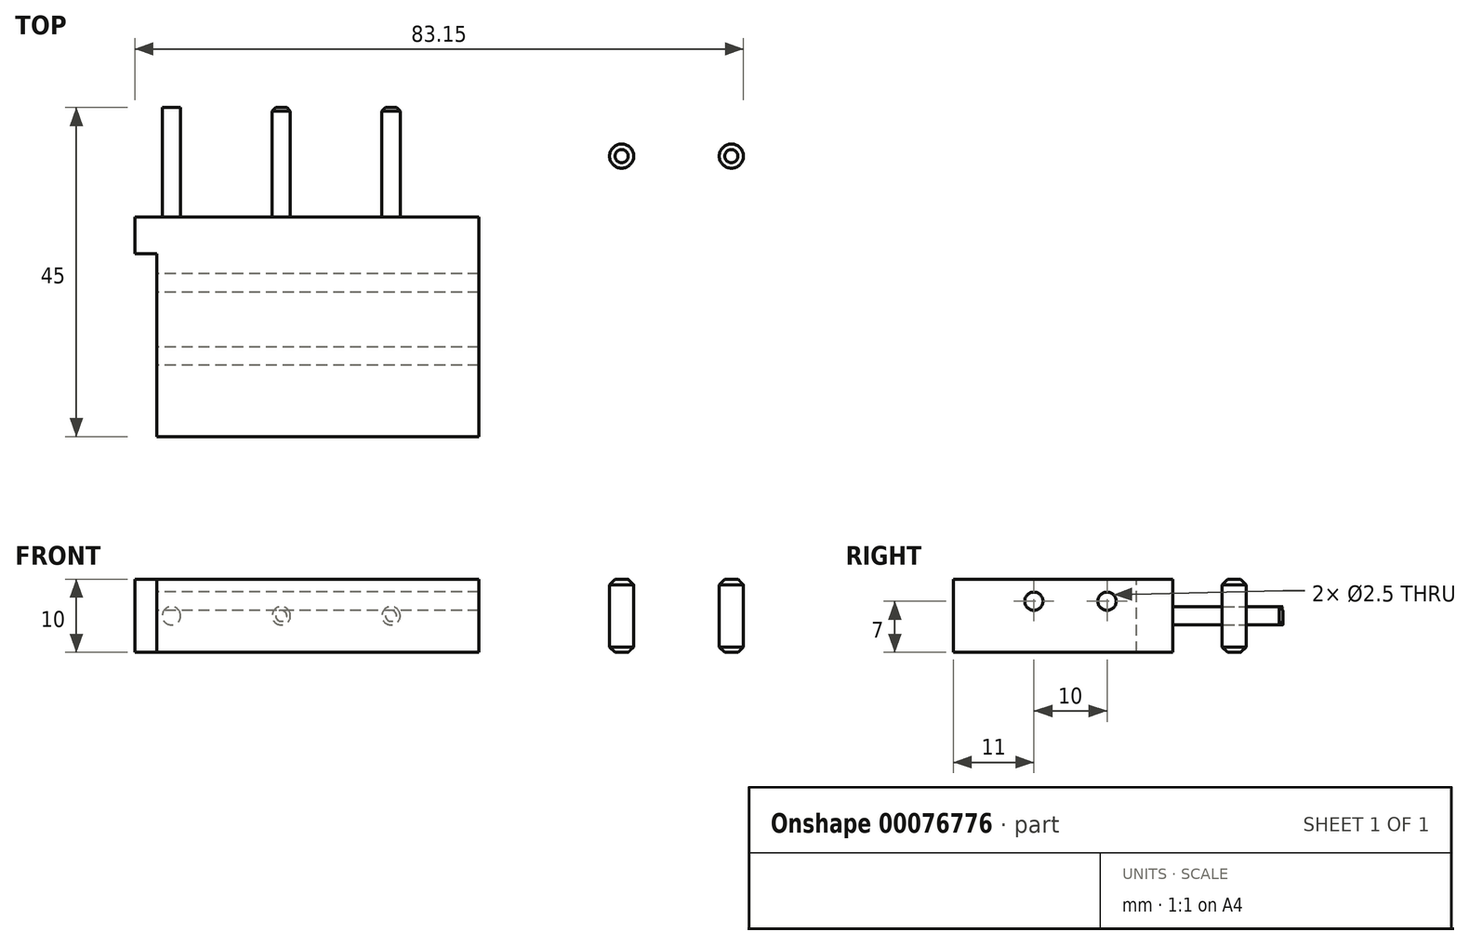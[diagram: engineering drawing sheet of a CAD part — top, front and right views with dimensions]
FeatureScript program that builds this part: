
annotation { "Feature Type Name" : "Feature", "Feature Type Description" : "" }
export const myFeature = defineFeature(function(context is Context, id is Id, definition is map)
    precondition{}
    {
        {
            var Q0;
            Q0=qCreatedBy(makeId("Top.planeOp"),FACE);
            var sketch = newSketch(context, id + "F0", { "sketchPlane" : qUnion([Q0])});
            skLineSegment(sketch, "E0.bottom", {"start": v(-44, 45) * mm, "end": v(44, 45) * mm});
            skLineSegment(sketch, "E0.top", {"start": v(-44, 0) * mm, "end": v(44, 0) * mm});
            skLineSegment(sketch, "E0.left", {"start": v(-44, 45) * mm, "end": v(-44, 0) * mm});
            skLineSegment(sketch, "E0.right", {"start": v(44, 45) * mm, "end": v(44, 0) * mm});
            skLineSegment(sketch, "E1", {"start": v(0, 45) * mm, "end": v(0, 0) * mm});
            skSolve(sketch);
        }
        {
            var Q0;
            {var subQ0=sQuery(id+"F0.wireOp",EDGE,"E0.left");Q0=makeQuery(id+"F0.imprint","IMPRINT",FACE,{"disambiguationData":[TD([[makeQuery(id+"F0.imprint","IMPRINT",EDGE,{"derivedFrom":subQ0}),1.0]])]});}
            var Q1;
            {var subQ0=sQuery(id+"F0.wireOp",EDGE,"E0.right");Q1=makeQuery(id+"F0.imprint","IMPRINT",FACE,{"disambiguationData":[TD([[makeQuery(id+"F0.imprint","IMPRINT",EDGE,{"derivedFrom":subQ0}),-1.0]])]});}
            extrude(context, id + "F1", {"entities" : qUnion([Q0, Q1]), "depth" : 10 * mm});
        }
        {
            var Q0;
            Q0=makeQuery(id+"F1.opExtrude","SWEPT_FACE",FACE,{"disambiguationData":[OSD([sQuery(id+"F0.wireOp",EDGE,"E0.left")])]});
            var sketch = newSketch(context, id + "F2", { "sketchPlane" : qUnion([Q0])});
            skCircle(sketch, "E2", {"center": v(-11, 7) * mm, "radius": 1.25 * mm});
            skCircle(sketch, "E3", {"center": v(-21, 7) * mm, "radius": 1.25 * mm});
            skSolve(sketch);
        }
        {
            var Q0;
            Q0=makeQuery(id+"F2.imprint","IMPRINT",FACE,{"disambiguationData":[TD([[makeQuery(id+"F2.imprint","IMPRINT",EDGE,{"derivedFrom":sQuery(id+"F2.wireOp",EDGE,"E3")}),1.0]])]});
            var Q1;
            Q1=makeQuery(id+"F2.imprint","IMPRINT",FACE,{"disambiguationData":[TD([[makeQuery(id+"F2.imprint","IMPRINT",EDGE,{"derivedFrom":sQuery(id+"F2.wireOp",EDGE,"E2")}),1.0]])]});
            extrude(context, id + "F3", {"entities" : qUnion([Q0, Q1]), "operationType" : NewBodyOperationType.REMOVE, "endBound" : BoundingType.THROUGH_ALL, "oppositeDirection" : true, "depth" : 25 * mm});
        }
        {
            var Q0;
            Q0=makeQuery(id+"F3.boolean.opBoolean","COPY",EDGE,{"derivedFrom":makeQuery(id+"F3.opExtrude","CAP_EDGE",EDGE,{"disambiguationData":[OSD([sQuery(id+"F2.wireOp",EDGE,"E3")])],"isStart":true})});
            var Q1;
            Q1=makeQuery(id+"F3.boolean.opBoolean","COPY",EDGE,{"derivedFrom":makeQuery(id+"F3.opExtrude","CAP_EDGE",EDGE,{"disambiguationData":[OSD([sQuery(id+"F2.wireOp",EDGE,"E2")])],"isStart":true})});
            var Q2;
            Q2=makeQuery(id+"F3.boolean.opBoolean","INTERSECT",EDGE,{"derivedFrom":[makeQuery(id+"F1.opExtrude","SWEPT_FACE",FACE,{"disambiguationData":[OSD([sQuery(id+"F0.wireOp",EDGE,"E0.right")])]}),makeQuery(id+"F3.opExtrude","SWEPT_FACE",FACE,{"disambiguationData":[OSD([sQuery(id+"F2.wireOp",EDGE,"E2")])]})]});
            var Q3;
            Q3=makeQuery(id+"F3.boolean.opBoolean","INTERSECT",EDGE,{"derivedFrom":[makeQuery(id+"F1.opExtrude","SWEPT_FACE",FACE,{"disambiguationData":[OSD([sQuery(id+"F0.wireOp",EDGE,"E0.right")])]}),makeQuery(id+"F3.opExtrude","SWEPT_FACE",FACE,{"disambiguationData":[OSD([sQuery(id+"F2.wireOp",EDGE,"E3")])]})]});
            chamfer(context, id + "F4", {"entities" : qUnion([Q0, Q1, Q2, Q3]), "width" : .5 * mm, "tangentPropagation" : true});
        }
        {
            var Q0;
            Q0=makeQuery(id+"F1.opExtrude","CAP_FACE",FACE,{"disambiguationData":[OSD([sQuery(id+"F0.wireOp",EDGE,"E0.bottom"),sQuery(id+"F0.wireOp",EDGE,"E0.top"),sQuery(id+"F0.wireOp",EDGE,"E0.left"),sQuery(id+"F0.wireOp",EDGE,"E0.right")])],"isStart":false});
            var sketch = newSketch(context, id + "F5", { "sketchPlane" : qUnion([Q0])});
            skLineSegment(sketch, "E4.bottom", {"start": v(-44, 45) * mm, "end": v(-47, 45) * mm});
            skLineSegment(sketch, "E4.top", {"start": v(-44, 25) * mm, "end": v(-47, 25) * mm});
            skLineSegment(sketch, "E4.left", {"start": v(-44, 45) * mm, "end": v(-44, 25) * mm});
            skLineSegment(sketch, "E4.right", {"start": v(-47, 45) * mm, "end": v(-47, 25) * mm});
            skLineSegment(sketch, "E5.bottom", {"start": v(44, 45) * mm, "end": v(47, 45) * mm});
            skLineSegment(sketch, "E5.top", {"start": v(44, 25) * mm, "end": v(47, 25) * mm});
            skLineSegment(sketch, "E5.left", {"start": v(44, 45) * mm, "end": v(44, 25) * mm});
            skLineSegment(sketch, "E5.right", {"start": v(47, 45) * mm, "end": v(47, 25) * mm});
            skSolve(sketch);
        }
        {
            var Q0;
            Q0=makeQuery(id+"F5.imprint","IMPRINT",FACE,{"disambiguationData":[TD([[makeQuery(id+"F5.imprint","IMPRINT",EDGE,{"derivedFrom":sQuery(id+"F5.wireOp",EDGE,"E4.bottom")}),1.0]])]});
            var Q1;
            Q1=makeQuery(id+"F5.imprint","IMPRINT",FACE,{"disambiguationData":[TD([[makeQuery(id+"F5.imprint","IMPRINT",EDGE,{"derivedFrom":sQuery(id+"F5.wireOp",EDGE,"E5.bottom")}),-1.0]])]});
            var Q2;
            Q2=makeQuery(id+"F1.opExtrude","CAP_FACE",FACE,{"disambiguationData":[OSD([sQuery(id+"F0.wireOp",EDGE,"E0.bottom"),sQuery(id+"F0.wireOp",EDGE,"E0.top"),sQuery(id+"F0.wireOp",EDGE,"E0.left"),sQuery(id+"F0.wireOp",EDGE,"E0.right")])],"isStart":true});
            extrude(context, id + "F6", {"entities" : qUnion([Q0, Q1]), "operationType" : NewBodyOperationType.ADD, "endBound" : BoundingType.UP_TO_SURFACE, "oppositeDirection" : true, "endBoundEntityFace" : qUnion([Q2]), "depth" : 25 * mm});
        }
        {
            var Q0;
            Q0=makeQuery(id+"F6.boolean.opBoolean","MERGE",FACE,{"derivedFrom":[makeQuery(id+"F1.opExtrude","CAP_FACE",FACE,{"disambiguationData":[OSD([sQuery(id+"F0.wireOp",EDGE,"E0.bottom"),sQuery(id+"F0.wireOp",EDGE,"E0.top"),sQuery(id+"F0.wireOp",EDGE,"E0.left"),sQuery(id+"F0.wireOp",EDGE,"E0.right")])],"isStart":false}),makeQuery(id+"F6.opExtrude","CAP_FACE",FACE,{"disambiguationData":[OSD([sQuery(id+"F5.wireOp",EDGE,"E4.bottom"),sQuery(id+"F5.wireOp",EDGE,"E4.top"),sQuery(id+"F5.wireOp",EDGE,"E4.left"),sQuery(id+"F5.wireOp",EDGE,"E4.right")])],"isStart":true}),makeQuery(id+"F6.opExtrude","CAP_FACE",FACE,{"disambiguationData":[OSD([sQuery(id+"F5.wireOp",EDGE,"E5.bottom"),sQuery(id+"F5.wireOp",EDGE,"E5.top"),sQuery(id+"F5.wireOp",EDGE,"E5.left"),sQuery(id+"F5.wireOp",EDGE,"E5.right")])],"isStart":true})]});
            var sketch = newSketch(context, id + "F7", { "sketchPlane" : qUnion([Q0])});
            skCircle(sketch, "E6", {"center": v(0, 34.5) * mm, "radius": 3.38 * mm});
            skCircle(sketch, "E7", {"center": v(-34.5, 38.35) * mm, "radius": 1.65 * mm});
            skLineSegment(sketch, "E8", {"start": v(0, 45) * mm, "end": v(0, 0) * mm});
            skCircle(sketch, "E9", {"center": v(-19.5, 38.35) * mm, "radius": 1.65 * mm});
            skLineSegment(sketch, "E10", {"start": v(-34.5, 38.35) * mm, "end": v(-19.5, 38.35) * mm});
            skCircle(sketch, "E11.MirrorC", {"center": v(19.5, 38.35) * mm, "radius": 1.65 * mm});
            skLineSegment(sketch, "E12.MirrorCS", {"start": v(34.5, 38.35) * mm, "end": v(19.5, 38.35) * mm});
            skCircle(sketch, "E13.MirrorC", {"center": v(34.5, 38.35) * mm, "radius": 1.65 * mm});
            skSolve(sketch);
        }
        {
            var Q0;
            Q0=makeQuery(id+"F7.imprint","IMPRINT",FACE,{"disambiguationData":[TD([[makeQuery(id+"F7.imprint","IMPRINT",EDGE,{"derivedFrom":sQuery(id+"F7.wireOp",EDGE,"E6")}),1.0]])]});
            var Q1;
            Q1=makeQuery(id+"F7.imprint","IMPRINT",FACE,{"disambiguationData":[TD([[makeQuery(id+"F7.imprint","IMPRINT",EDGE,{"derivedFrom":sQuery(id+"F7.wireOp",EDGE,"E7")}),1.0]])]});
            var Q2;
            Q2=makeQuery(id+"F7.imprint","IMPRINT",FACE,{"disambiguationData":[TD([[makeQuery(id+"F7.imprint","IMPRINT",EDGE,{"derivedFrom":sQuery(id+"F7.wireOp",EDGE,"E9")}),1.0]])]});
            var Q3;
            Q3=makeQuery(id+"F7.imprint","IMPRINT",FACE,{"disambiguationData":[TD([[makeQuery(id+"F7.imprint","IMPRINT",EDGE,{"derivedFrom":sQuery(id+"F7.wireOp",EDGE,"E11.MirrorC")}),-1.0]])]});
            var Q4;
            Q4=makeQuery(id+"F7.imprint","IMPRINT",FACE,{"disambiguationData":[TD([[makeQuery(id+"F7.imprint","IMPRINT",EDGE,{"derivedFrom":sQuery(id+"F7.wireOp",EDGE,"E13.MirrorC")}),-1.0]])]});
            extrude(context, id + "F8", {"entities" : qUnion([Q0, Q1, Q2, Q3, Q4]), "operationType" : NewBodyOperationType.REMOVE, "endBound" : BoundingType.THROUGH_ALL, "oppositeDirection" : true, "depth" : 25 * mm});
        }
        {
            var Q0;
            Q0=makeQuery(id+"F8.boolean.opBoolean","COPY",EDGE,{"derivedFrom":makeQuery(id+"F8.opExtrude","CAP_EDGE",EDGE,{"disambiguationData":[OSD([sQuery(id+"F7.wireOp",EDGE,"E6")])],"isStart":true})});
            var Q1;
            {var subQ0=sQuery(id+"F0.wireOp",EDGE,"E0.right");var subQ1=sQuery(id+"F0.wireOp",EDGE,"E0.left");var subQ2=sQuery(id+"F0.wireOp",EDGE,"E0.top");var subQ3=sQuery(id+"F0.wireOp",EDGE,"E0.bottom");Q1=makeQuery(id+"F8.boolean.opBoolean","INTERSECT",EDGE,{"derivedFrom":[makeQuery(id+"F6.boolean.opBoolean","MERGE",FACE,{"derivedFrom":[makeQuery(id+"F1.opExtrude","CAP_FACE",FACE,{"disambiguationData":[OSD([subQ3,subQ2,subQ1,subQ0])],"isStart":true}),makeQuery(id+"F6.opExtrude","CAP_FACE",FACE,{"disambiguationData":[OSD([subQ3,subQ2,subQ1,subQ0]),ownerDisambiguation([makeQuery(id+"F6.opExtrude","SWEPT_BODY",BODY,{"disambiguationData":[OSD([sQuery(id+"F5.wireOp",EDGE,"E4.bottom"),sQuery(id+"F5.wireOp",EDGE,"E4.top"),sQuery(id+"F5.wireOp",EDGE,"E4.left"),sQuery(id+"F5.wireOp",EDGE,"E4.right")])]})])],"isStart":false}),makeQuery(id+"F6.opExtrude","CAP_FACE",FACE,{"disambiguationData":[OSD([subQ3,subQ2,subQ1,subQ0]),ownerDisambiguation([makeQuery(id+"F6.opExtrude","SWEPT_BODY",BODY,{"disambiguationData":[OSD([sQuery(id+"F5.wireOp",EDGE,"E5.bottom"),sQuery(id+"F5.wireOp",EDGE,"E5.top"),sQuery(id+"F5.wireOp",EDGE,"E5.left"),sQuery(id+"F5.wireOp",EDGE,"E5.right")])]})])],"isStart":false})]}),makeQuery(id+"F8.opExtrude","SWEPT_FACE",FACE,{"disambiguationData":[OSD([sQuery(id+"F7.wireOp",EDGE,"E6")])]})]});}
            var Q2;
            Q2=makeQuery(id+"F8.boolean.opBoolean","COPY",EDGE,{"derivedFrom":makeQuery(id+"F8.opExtrude","CAP_EDGE",EDGE,{"disambiguationData":[OSD([sQuery(id+"F7.wireOp",EDGE,"E7")])],"isStart":true})});
            var Q3;
            Q3=makeQuery(id+"F8.boolean.opBoolean","COPY",EDGE,{"derivedFrom":makeQuery(id+"F8.opExtrude","CAP_EDGE",EDGE,{"disambiguationData":[OSD([sQuery(id+"F7.wireOp",EDGE,"E9")])],"isStart":true})});
            var Q4;
            Q4=makeQuery(id+"F8.boolean.opBoolean","COPY",EDGE,{"derivedFrom":makeQuery(id+"F8.opExtrude","CAP_EDGE",EDGE,{"disambiguationData":[OSD([sQuery(id+"F7.wireOp",EDGE,"E11.MirrorC")])],"isStart":true})});
            var Q5;
            Q5=makeQuery(id+"F8.boolean.opBoolean","COPY",EDGE,{"derivedFrom":makeQuery(id+"F8.opExtrude","CAP_EDGE",EDGE,{"disambiguationData":[OSD([sQuery(id+"F7.wireOp",EDGE,"E13.MirrorC")])],"isStart":true})});
            var Q6;
            {var subQ0=sQuery(id+"F0.wireOp",EDGE,"E0.right");var subQ1=sQuery(id+"F0.wireOp",EDGE,"E0.left");var subQ2=sQuery(id+"F0.wireOp",EDGE,"E0.top");var subQ3=sQuery(id+"F0.wireOp",EDGE,"E0.bottom");Q6=makeQuery(id+"F8.boolean.opBoolean","INTERSECT",EDGE,{"derivedFrom":[makeQuery(id+"F6.boolean.opBoolean","MERGE",FACE,{"derivedFrom":[makeQuery(id+"F1.opExtrude","CAP_FACE",FACE,{"disambiguationData":[OSD([subQ3,subQ2,subQ1,subQ0])],"isStart":true}),makeQuery(id+"F6.opExtrude","CAP_FACE",FACE,{"disambiguationData":[OSD([subQ3,subQ2,subQ1,subQ0]),ownerDisambiguation([makeQuery(id+"F6.opExtrude","SWEPT_BODY",BODY,{"disambiguationData":[OSD([sQuery(id+"F5.wireOp",EDGE,"E4.bottom"),sQuery(id+"F5.wireOp",EDGE,"E4.top"),sQuery(id+"F5.wireOp",EDGE,"E4.left"),sQuery(id+"F5.wireOp",EDGE,"E4.right")])]})])],"isStart":false}),makeQuery(id+"F6.opExtrude","CAP_FACE",FACE,{"disambiguationData":[OSD([subQ3,subQ2,subQ1,subQ0]),ownerDisambiguation([makeQuery(id+"F6.opExtrude","SWEPT_BODY",BODY,{"disambiguationData":[OSD([sQuery(id+"F5.wireOp",EDGE,"E5.bottom"),sQuery(id+"F5.wireOp",EDGE,"E5.top"),sQuery(id+"F5.wireOp",EDGE,"E5.left"),sQuery(id+"F5.wireOp",EDGE,"E5.right")])]})])],"isStart":false})]}),makeQuery(id+"F8.opExtrude","SWEPT_FACE",FACE,{"disambiguationData":[OSD([sQuery(id+"F7.wireOp",EDGE,"E13.MirrorC")])]})]});}
            var Q7;
            {var subQ0=sQuery(id+"F0.wireOp",EDGE,"E0.right");var subQ1=sQuery(id+"F0.wireOp",EDGE,"E0.left");var subQ2=sQuery(id+"F0.wireOp",EDGE,"E0.top");var subQ3=sQuery(id+"F0.wireOp",EDGE,"E0.bottom");Q7=makeQuery(id+"F8.boolean.opBoolean","INTERSECT",EDGE,{"derivedFrom":[makeQuery(id+"F6.boolean.opBoolean","MERGE",FACE,{"derivedFrom":[makeQuery(id+"F1.opExtrude","CAP_FACE",FACE,{"disambiguationData":[OSD([subQ3,subQ2,subQ1,subQ0])],"isStart":true}),makeQuery(id+"F6.opExtrude","CAP_FACE",FACE,{"disambiguationData":[OSD([subQ3,subQ2,subQ1,subQ0]),ownerDisambiguation([makeQuery(id+"F6.opExtrude","SWEPT_BODY",BODY,{"disambiguationData":[OSD([sQuery(id+"F5.wireOp",EDGE,"E4.bottom"),sQuery(id+"F5.wireOp",EDGE,"E4.top"),sQuery(id+"F5.wireOp",EDGE,"E4.left"),sQuery(id+"F5.wireOp",EDGE,"E4.right")])]})])],"isStart":false}),makeQuery(id+"F6.opExtrude","CAP_FACE",FACE,{"disambiguationData":[OSD([subQ3,subQ2,subQ1,subQ0]),ownerDisambiguation([makeQuery(id+"F6.opExtrude","SWEPT_BODY",BODY,{"disambiguationData":[OSD([sQuery(id+"F5.wireOp",EDGE,"E5.bottom"),sQuery(id+"F5.wireOp",EDGE,"E5.top"),sQuery(id+"F5.wireOp",EDGE,"E5.left"),sQuery(id+"F5.wireOp",EDGE,"E5.right")])]})])],"isStart":false})]}),makeQuery(id+"F8.opExtrude","SWEPT_FACE",FACE,{"disambiguationData":[OSD([sQuery(id+"F7.wireOp",EDGE,"E11.MirrorC")])]})]});}
            var Q8;
            {var subQ0=sQuery(id+"F0.wireOp",EDGE,"E0.right");var subQ1=sQuery(id+"F0.wireOp",EDGE,"E0.left");var subQ2=sQuery(id+"F0.wireOp",EDGE,"E0.top");var subQ3=sQuery(id+"F0.wireOp",EDGE,"E0.bottom");Q8=makeQuery(id+"F8.boolean.opBoolean","INTERSECT",EDGE,{"derivedFrom":[makeQuery(id+"F6.boolean.opBoolean","MERGE",FACE,{"derivedFrom":[makeQuery(id+"F1.opExtrude","CAP_FACE",FACE,{"disambiguationData":[OSD([subQ3,subQ2,subQ1,subQ0])],"isStart":true}),makeQuery(id+"F6.opExtrude","CAP_FACE",FACE,{"disambiguationData":[OSD([subQ3,subQ2,subQ1,subQ0]),ownerDisambiguation([makeQuery(id+"F6.opExtrude","SWEPT_BODY",BODY,{"disambiguationData":[OSD([sQuery(id+"F5.wireOp",EDGE,"E4.bottom"),sQuery(id+"F5.wireOp",EDGE,"E4.top"),sQuery(id+"F5.wireOp",EDGE,"E4.left"),sQuery(id+"F5.wireOp",EDGE,"E4.right")])]})])],"isStart":false}),makeQuery(id+"F6.opExtrude","CAP_FACE",FACE,{"disambiguationData":[OSD([subQ3,subQ2,subQ1,subQ0]),ownerDisambiguation([makeQuery(id+"F6.opExtrude","SWEPT_BODY",BODY,{"disambiguationData":[OSD([sQuery(id+"F5.wireOp",EDGE,"E5.bottom"),sQuery(id+"F5.wireOp",EDGE,"E5.top"),sQuery(id+"F5.wireOp",EDGE,"E5.left"),sQuery(id+"F5.wireOp",EDGE,"E5.right")])]})])],"isStart":false})]}),makeQuery(id+"F8.opExtrude","SWEPT_FACE",FACE,{"disambiguationData":[OSD([sQuery(id+"F7.wireOp",EDGE,"E9")])]})]});}
            var Q9;
            {var subQ0=sQuery(id+"F0.wireOp",EDGE,"E0.right");var subQ1=sQuery(id+"F0.wireOp",EDGE,"E0.left");var subQ2=sQuery(id+"F0.wireOp",EDGE,"E0.top");var subQ3=sQuery(id+"F0.wireOp",EDGE,"E0.bottom");Q9=makeQuery(id+"F8.boolean.opBoolean","INTERSECT",EDGE,{"derivedFrom":[makeQuery(id+"F6.boolean.opBoolean","MERGE",FACE,{"derivedFrom":[makeQuery(id+"F1.opExtrude","CAP_FACE",FACE,{"disambiguationData":[OSD([subQ3,subQ2,subQ1,subQ0])],"isStart":true}),makeQuery(id+"F6.opExtrude","CAP_FACE",FACE,{"disambiguationData":[OSD([subQ3,subQ2,subQ1,subQ0]),ownerDisambiguation([makeQuery(id+"F6.opExtrude","SWEPT_BODY",BODY,{"disambiguationData":[OSD([sQuery(id+"F5.wireOp",EDGE,"E4.bottom"),sQuery(id+"F5.wireOp",EDGE,"E4.top"),sQuery(id+"F5.wireOp",EDGE,"E4.left"),sQuery(id+"F5.wireOp",EDGE,"E4.right")])]})])],"isStart":false}),makeQuery(id+"F6.opExtrude","CAP_FACE",FACE,{"disambiguationData":[OSD([subQ3,subQ2,subQ1,subQ0]),ownerDisambiguation([makeQuery(id+"F6.opExtrude","SWEPT_BODY",BODY,{"disambiguationData":[OSD([sQuery(id+"F5.wireOp",EDGE,"E5.bottom"),sQuery(id+"F5.wireOp",EDGE,"E5.top"),sQuery(id+"F5.wireOp",EDGE,"E5.left"),sQuery(id+"F5.wireOp",EDGE,"E5.right")])]})])],"isStart":false})]}),makeQuery(id+"F8.opExtrude","SWEPT_FACE",FACE,{"disambiguationData":[OSD([sQuery(id+"F7.wireOp",EDGE,"E7")])]})]});}
            chamfer(context, id + "F9", {"entities" : qUnion([Q0, Q1, Q2, Q3, Q4, Q5, Q6, Q7, Q8, Q9]), "width" : .75 * mm, "tangentPropagation" : true});
        }
        {
            var Q0;
            Q0=makeQuery(id+"F6.boolean.opBoolean","MERGE",FACE,{"derivedFrom":[makeQuery(id+"F1.opExtrude","SWEPT_FACE",FACE,{"disambiguationData":[OSD([sQuery(id+"F0.wireOp",EDGE,"E0.bottom")])]}),makeQuery(id+"F6.opExtrude","SWEPT_FACE",FACE,{"disambiguationData":[OSD([sQuery(id+"F5.wireOp",EDGE,"E4.bottom")])]}),makeQuery(id+"F6.opExtrude","SWEPT_FACE",FACE,{"disambiguationData":[OSD([sQuery(id+"F5.wireOp",EDGE,"E5.bottom")])]})]});
            var sketch = newSketch(context, id + "F10", { "sketchPlane" : qUnion([Q0])});
            skCircle(sketch, "E14", {"center": v(-42, 5) * mm, "radius": 1.25 * mm});
            skPoint(sketch, "E14.centerSnap0", {"position": v(-47, 5) * mm});
            skLineSegment(sketch, "E15", {"start": v(0, 0) * mm, "end": v(0, 10) * mm});
            skCircle(sketch, "E16.MirrorC", {"center": v(42, 5) * mm, "radius": 1.25 * mm});
            skCircle(sketch, "E17", {"center": v(-27, 5) * mm, "radius": 1.25 * mm});
            skCircle(sketch, "E18", {"center": v(-12, 5) * mm, "radius": 1.25 * mm});
            skCircle(sketch, "E19.MirrorC", {"center": v(12, 5) * mm, "radius": 1.25 * mm});
            skCircle(sketch, "E20.MirrorC", {"center": v(27, 5) * mm, "radius": 1.25 * mm});
            skSolve(sketch);
        }
        {
            var Q0;
            Q0=makeQuery(id+"F10.imprint","IMPRINT",FACE,{"disambiguationData":[TD([[makeQuery(id+"F10.imprint","IMPRINT",EDGE,{"derivedFrom":sQuery(id+"F10.wireOp",EDGE,"E14")}),1.0]])]});
            var Q1;
            Q1=makeQuery(id+"F10.imprint","IMPRINT",FACE,{"disambiguationData":[TD([[makeQuery(id+"F10.imprint","IMPRINT",EDGE,{"derivedFrom":sQuery(id+"F10.wireOp",EDGE,"E16.MirrorC")}),-1.0]])]});
            var Q2;
            Q2=makeQuery(id+"F10.imprint","IMPRINT",FACE,{"disambiguationData":[TD([[makeQuery(id+"F10.imprint","IMPRINT",EDGE,{"derivedFrom":sQuery(id+"F10.wireOp",EDGE,"E17")}),1.0]])]});
            var Q3;
            Q3=makeQuery(id+"F10.imprint","IMPRINT",FACE,{"disambiguationData":[TD([[makeQuery(id+"F10.imprint","IMPRINT",EDGE,{"derivedFrom":sQuery(id+"F10.wireOp",EDGE,"E18")}),1.0]])]});
            var Q4;
            Q4=makeQuery(id+"F10.imprint","IMPRINT",FACE,{"disambiguationData":[TD([[makeQuery(id+"F10.imprint","IMPRINT",EDGE,{"derivedFrom":sQuery(id+"F10.wireOp",EDGE,"E19.MirrorC")}),-1.0]])]});
            var Q5;
            Q5=makeQuery(id+"F10.imprint","IMPRINT",FACE,{"disambiguationData":[TD([[makeQuery(id+"F10.imprint","IMPRINT",EDGE,{"derivedFrom":sQuery(id+"F10.wireOp",EDGE,"E20.MirrorC")}),-1.0]])]});
            extrude(context, id + "F11", {"entities" : qUnion([Q0, Q1, Q2, Q3, Q4, Q5]), "operationType" : NewBodyOperationType.REMOVE, "oppositeDirection" : true, "depth" : 15 * mm});
        }
        {
            var Q0;
            Q0=makeQuery(id+"F11.boolean.opBoolean","COPY",EDGE,{"derivedFrom":makeQuery(id+"F11.opExtrude","CAP_EDGE",EDGE,{"disambiguationData":[OSD([sQuery(id+"F10.wireOp",EDGE,"E14")])],"isStart":true})});
            var Q1;
            Q1=makeQuery(id+"F11.boolean.opBoolean","COPY",EDGE,{"derivedFrom":makeQuery(id+"F11.opExtrude","CAP_EDGE",EDGE,{"disambiguationData":[OSD([sQuery(id+"F10.wireOp",EDGE,"E16.MirrorC")])],"isStart":true})});
            var Q2;
            Q2=makeQuery(id+"F11.boolean.opBoolean","COPY",EDGE,{"derivedFrom":makeQuery(id+"F11.opExtrude","CAP_EDGE",EDGE,{"disambiguationData":[OSD([sQuery(id+"F10.wireOp",EDGE,"E17")])],"isStart":true})});
            var Q3;
            Q3=makeQuery(id+"F11.boolean.opBoolean","COPY",EDGE,{"derivedFrom":makeQuery(id+"F11.opExtrude","CAP_EDGE",EDGE,{"disambiguationData":[OSD([sQuery(id+"F10.wireOp",EDGE,"E18")])],"isStart":true})});
            var Q4;
            Q4=makeQuery(id+"F11.boolean.opBoolean","COPY",EDGE,{"derivedFrom":makeQuery(id+"F11.opExtrude","CAP_EDGE",EDGE,{"disambiguationData":[OSD([sQuery(id+"F10.wireOp",EDGE,"E19.MirrorC")])],"isStart":true})});
            var Q5;
            Q5=makeQuery(id+"F11.boolean.opBoolean","COPY",EDGE,{"derivedFrom":makeQuery(id+"F11.opExtrude","CAP_EDGE",EDGE,{"disambiguationData":[OSD([sQuery(id+"F10.wireOp",EDGE,"E20.MirrorC")])],"isStart":true})});
            chamfer(context, id + "F12", {"entities" : qUnion([Q0, Q1, Q2, Q3, Q4, Q5]), "width" : .5 * mm, "tangentPropagation" : true});
        }
    });
